# Revit family: 0032004
name_source: partatom
category: Lighting Fixtures
revit_build: Autodesk Revit 2017 (Build: 20160225_1515(x64)
units: mm (PartAtom-declared; Revit-internal decimal feet)

## family parameters
Cut with Voids When Loaded = No
Host = Face
Light Source = Yes
OmniClass Number = 23.80.70.00
OmniClass Title = Lighting
Part Type = Normal
Room Calculation Point = No
Round Connector Dimension = Use Diameter
Shared = No

## types (2) — shared parameters
Assembly Code = D5020200
AssetType = Fixed
ClassificationName = Uniclass2015
ClassificationValue = EF_70_80
Color Filter = 16777215
Default Elevation = 1219 mm
Dimming Lamp Color Temperature Shift = <None>
DimmingControlOptions = Non dimmable
DocumentationLiterature = http://www.sylvania-lighting.com
DurationUnit = hours
ElectricShockClassification = Class II
Emit Shape Visible in Rendering = No
Emit from Rectangle Length = 320 mm  [stored 1.04987 ft]
Emit from Rectangle Width = 95 mm
ExpectedLife = 50000
IfcExportAs = IfcLightFixtureType
IfcExportType = IfcLightFixtureType
IngressProtection = IP65
Keynote = 16500
Lamp = LED
LampColourTemperature = 6500 K
LampsType = LED
LuminousEfficacy = 46.53 lm/W
Manufacturer = Feilo Sylvania
ManufacturerName = Feilo Sylvania
Material_1_SYL = PC/ABS Plastic
Material_2_SYL = Plastic, Transparent
Material_3_SYL = LED-Sylvania
Model = START eco Emergency Bulkhead MT M/NM 3h 170lm
ModelNumber = 0032004
ModelReference = START eco Emergency Bulkhead MT M/NM 3h 170lm
Name = START eco Emergency Bulkhead MT M/NM 3h 170lm
NominalDepth = 110 mm  [stored 0.360892 ft]
NominalHeight = 60 mm
NominalLength = 346 mm
Tilt Angle = -90.00°
Type Image = <None>
URL = http://www.sylvania-lighting.com
Weight = 6.96 kg
zero-valued in all types: Cost, PowerFactor

## per-type parameters (varying)
| type | Apparent Load | InputNominalFrequency | InputVoltage | LampNominalLuminous | Photometric Web File | PowerConsumption | TypeName | Voltage |
| 0032004 ST E EM BULKHEAD MT M/NM 3H 170LM Emergency mode | 0 VA |  |  | 175 lm | 0032004EM.ies | 0 W | START eco Emergency Bulkhead MT M/NM 3h 170lm Emergency mode | 0 V |
| 0032004 ST E EM BULKHEAD MT M/NM 3H 170LM | 4 VA | 50/60 Hz | 230-240V~ | 177 lm | 0032004.ies | 3.6 W | START eco Emergency Bulkhead MT M/NM 3h 170lm | 230 V |

note: [stored X ft] marks values corroborated as IEEE doubles in the binary element streams (Revit-internal decimal feet)

## geometry (parser evidence)
native form markers: Sweep x3
no freeform markers — native parametric forms only
